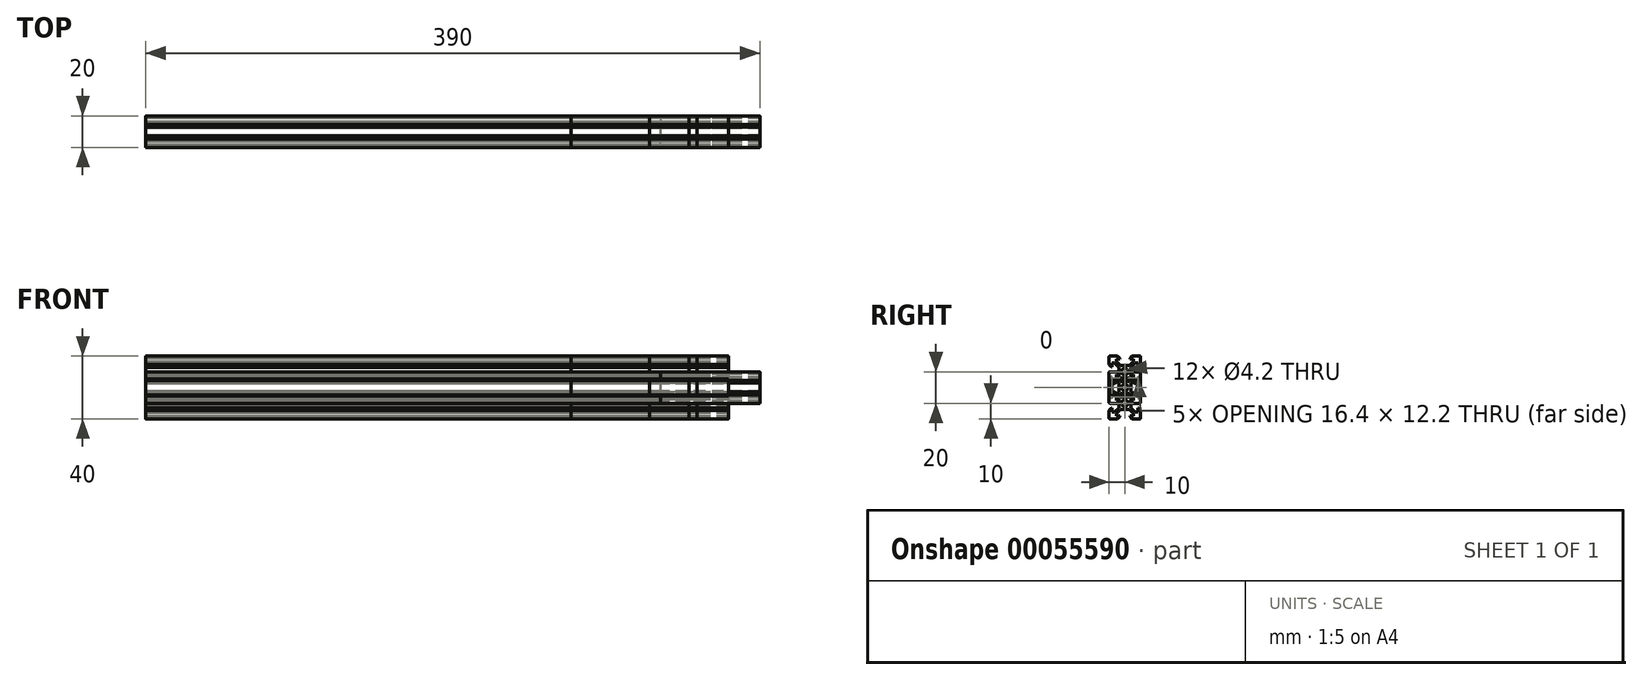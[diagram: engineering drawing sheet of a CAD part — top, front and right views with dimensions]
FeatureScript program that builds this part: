
annotation { "Feature Type Name" : "Feature", "Feature Type Description" : "" }
export const myFeature = defineFeature(function(context is Context, id is Id, definition is map)
    precondition{}
    {
        {
            var Q0;
            Q0=qCreatedBy(makeId("Right.planeOp"),FACE);
            var sketch = newSketch(context, id + "F0", { "sketchPlane" : qUnion([Q0]), "asVersion" : FeatureScriptVersionNumber.V275_SKETCH_PATTERN_LOWER_LIMIT});
            skLineSegment(sketch, "E0", {"start": v(0, 13.9) * mm, "end": v(-2.84, 13.9) * mm});
            skLineSegment(sketch, "E1", {"start": v(-2.84, 13.9) * mm, "end": v(-5.5, 16.56) * mm});
            skLineSegment(sketch, "E2", {"start": v(-5.5, 16.56) * mm, "end": v(-5.5, 18.2) * mm});
            skLineSegment(sketch, "E3", {"start": v(-5.5, 18.2) * mm, "end": v(-3.13, 18.2) * mm});
            skLineSegment(sketch, "E4", {"start": v(-3.13, 18.2) * mm, "end": v(-3.13, 18.55) * mm});
            skLineSegment(sketch, "E5", {"start": v(-3.13, 18.55) * mm, "end": v(-4.58, 20) * mm});
            skLineSegment(sketch, "E6", {"start": v(-4.58, 20) * mm, "end": v(-9.5, 20) * mm});
            skLineSegment(sketch, "E7", {"start": v(-10, 20) * mm, "end": v(0, 10) * mm, "construction": true});
            skLineSegment(sketch, "E8.MirrorCS", {"start": v(-3.9, 10) * mm, "end": v(-3.9, 12.84) * mm});
            skLineSegment(sketch, "E9.MirrorCS", {"start": v(-3.9, 12.84) * mm, "end": v(-6.56, 15.5) * mm});
            skLineSegment(sketch, "E10.MirrorCS", {"start": v(-6.56, 15.5) * mm, "end": v(-8.2, 15.5) * mm});
            skLineSegment(sketch, "E11.MirrorCS", {"start": v(-8.2, 15.5) * mm, "end": v(-8.2, 13.13) * mm});
            skLineSegment(sketch, "E12.MirrorCS", {"start": v(-8.2, 13.12) * mm, "end": v(-8.55, 13.12) * mm});
            skLineSegment(sketch, "E13.MirrorCS", {"start": v(-8.55, 13.13) * mm, "end": v(-10, 14.58) * mm});
            skLineSegment(sketch, "E14.MirrorCS", {"start": v(-10, 14.58) * mm, "end": v(-10, 19.5) * mm});
            skCircle(sketch, "E15", {"center": v(0, 10) * mm, "radius": 2.1 * mm});
            skPoint(sketch, "E16.visualSharp", {"position": v(-10, 20) * mm});
            skArc(sketch, "E16.filletArc", {"start": v(-9.5, 20) * mm, "mid": v(-9.85, 19.85) * mm, "end": v(-10, 19.5) * mm});
            skLineSegment(sketch, "E17", {"start": v(0, 10) * mm, "end": v(-3.9, 10) * mm, "construction": true});
            skLineSegment(sketch, "E18.MirrorCS", {"start": v(-3.9, 10) * mm, "end": v(-3.9, 7.16) * mm});
            skLineSegment(sketch, "E19.MirrorCS", {"start": v(0, 6.1) * mm, "end": v(-2.84, 6.1) * mm});
            skLineSegment(sketch, "E20.MirrorCS", {"start": v(-3.9, 7.16) * mm, "end": v(-6.56, 4.5) * mm});
            skLineSegment(sketch, "E21.MirrorCS", {"start": v(-6.56, 4.5) * mm, "end": v(-8.2, 4.5) * mm});
            skLineSegment(sketch, "E22.MirrorCS", {"start": v(-8.2, 4.5) * mm, "end": v(-8.2, 6.87) * mm});
            skLineSegment(sketch, "E23.MirrorCS", {"start": v(-8.2, 6.87) * mm, "end": v(-8.55, 6.87) * mm});
            skLineSegment(sketch, "E24.MirrorCS", {"start": v(-8.55, 6.87) * mm, "end": v(-10, 5.42) * mm});
            skLineSegment(sketch, "E25", {"start": v(-10, 5.42) * mm, "end": v(-10, 0) * mm});
            skLineSegment(sketch, "E26", {"start": v(-2.84, 6.1) * mm, "end": v(-6.24, 2.7) * mm});
            skLineSegment(sketch, "E27", {"start": v(-6.24, 2.7) * mm, "end": v(-8.2, 2.7) * mm});
            skLineSegment(sketch, "E28", {"start": v(-8.2, 2.7) * mm, "end": v(-8.2, 0) * mm});
            skLineSegment(sketch, "E29.MirrorCS", {"start": v(0, 13.9) * mm, "end": v(2.84, 13.9) * mm});
            skLineSegment(sketch, "E30.MirrorCS", {"start": v(2.84, 13.9) * mm, "end": v(5.5, 16.56) * mm});
            skLineSegment(sketch, "E31.MirrorCS", {"start": v(5.5, 16.56) * mm, "end": v(5.5, 18.2) * mm});
            skLineSegment(sketch, "E32.MirrorCS", {"start": v(5.5, 18.2) * mm, "end": v(3.13, 18.2) * mm});
            skLineSegment(sketch, "E33.MirrorCS", {"start": v(3.13, 18.2) * mm, "end": v(3.13, 18.55) * mm});
            skLineSegment(sketch, "E34.MirrorCS", {"start": v(3.13, 18.55) * mm, "end": v(4.58, 20) * mm});
            skLineSegment(sketch, "E35.MirrorCS", {"start": v(4.58, 20) * mm, "end": v(9.5, 20) * mm});
            skArc(sketch, "E36.MirrorCS", {"start": v(9.5, 20) * mm, "mid": v(9.85, 19.85) * mm, "end": v(10, 19.5) * mm});
            skLineSegment(sketch, "E37.MirrorCS", {"start": v(10, 14.58) * mm, "end": v(10, 19.5) * mm});
            skLineSegment(sketch, "E38.MirrorCS", {"start": v(8.55, 13.13) * mm, "end": v(10, 14.58) * mm});
            skLineSegment(sketch, "E39.MirrorCS", {"start": v(8.2, 13.12) * mm, "end": v(8.55, 13.12) * mm});
            skLineSegment(sketch, "E40.MirrorCS", {"start": v(8.2, 15.5) * mm, "end": v(8.2, 13.13) * mm});
            skLineSegment(sketch, "E41.MirrorCS", {"start": v(6.56, 15.5) * mm, "end": v(8.2, 15.5) * mm});
            skLineSegment(sketch, "E42.MirrorCS", {"start": v(3.9, 12.84) * mm, "end": v(6.56, 15.5) * mm});
            skLineSegment(sketch, "E43.MirrorCS", {"start": v(3.9, 10) * mm, "end": v(3.9, 12.84) * mm});
            skLineSegment(sketch, "E44.MirrorCS", {"start": v(3.9, 10) * mm, "end": v(3.9, 7.16) * mm});
            skLineSegment(sketch, "E45.MirrorCS", {"start": v(3.9, 7.16) * mm, "end": v(6.56, 4.5) * mm});
            skLineSegment(sketch, "E46.MirrorCS", {"start": v(6.56, 4.5) * mm, "end": v(8.2, 4.5) * mm});
            skLineSegment(sketch, "E47.MirrorCS", {"start": v(8.2, 4.5) * mm, "end": v(8.2, 6.87) * mm});
            skLineSegment(sketch, "E48.MirrorCS", {"start": v(8.2, 6.87) * mm, "end": v(8.55, 6.87) * mm});
            skLineSegment(sketch, "E49.MirrorCS", {"start": v(8.55, 6.87) * mm, "end": v(10, 5.42) * mm});
            skLineSegment(sketch, "E50.MirrorCS", {"start": v(10, 5.42) * mm, "end": v(10, 0) * mm});
            skLineSegment(sketch, "E51.MirrorCS", {"start": v(0, 6.1) * mm, "end": v(2.84, 6.1) * mm});
            skLineSegment(sketch, "E52.MirrorCS", {"start": v(2.84, 6.1) * mm, "end": v(6.24, 2.7) * mm});
            skLineSegment(sketch, "E53.MirrorCS", {"start": v(6.24, 2.7) * mm, "end": v(8.2, 2.7) * mm});
            skLineSegment(sketch, "E54.MirrorCS", {"start": v(8.2, 2.7) * mm, "end": v(8.2, 0) * mm});
            skLineSegment(sketch, "E55.MirrorCS", {"start": v(8.2, -2.7) * mm, "end": v(8.2, 0) * mm});
            skLineSegment(sketch, "E56.MirrorCS", {"start": v(6.24, -2.7) * mm, "end": v(8.2, -2.7) * mm});
            skLineSegment(sketch, "E57.MirrorCS", {"start": v(2.84, -6.1) * mm, "end": v(6.24, -2.7) * mm});
            skLineSegment(sketch, "E58.MirrorCS", {"start": v(0, -6.1) * mm, "end": v(2.84, -6.1) * mm});
            skLineSegment(sketch, "E59.MirrorCS", {"start": v(0, -6.1) * mm, "end": v(-2.84, -6.1) * mm});
            skLineSegment(sketch, "E60.MirrorCS", {"start": v(-2.84, -6.1) * mm, "end": v(-6.24, -2.7) * mm});
            skLineSegment(sketch, "E61.MirrorCS", {"start": v(-6.24, -2.7) * mm, "end": v(-8.2, -2.7) * mm});
            skLineSegment(sketch, "E62.MirrorCS", {"start": v(-8.2, -2.7) * mm, "end": v(-8.2, 0) * mm});
            skLineSegment(sketch, "E63.MirrorCS", {"start": v(10, -5.42) * mm, "end": v(10, 0) * mm});
            skLineSegment(sketch, "E64.MirrorCS", {"start": v(8.55, -6.87) * mm, "end": v(10, -5.42) * mm});
            skLineSegment(sketch, "E65.MirrorCS", {"start": v(8.2, -6.87) * mm, "end": v(8.55, -6.87) * mm});
            skLineSegment(sketch, "E66.MirrorCS", {"start": v(8.2, -4.5) * mm, "end": v(8.2, -6.87) * mm});
            skLineSegment(sketch, "E67.MirrorCS", {"start": v(6.56, -4.5) * mm, "end": v(8.2, -4.5) * mm});
            skLineSegment(sketch, "E68.MirrorCS", {"start": v(3.9, -7.16) * mm, "end": v(6.56, -4.5) * mm});
            skLineSegment(sketch, "E69.MirrorCS", {"start": v(3.9, -10) * mm, "end": v(3.9, -7.16) * mm});
            skLineSegment(sketch, "E70.MirrorCS", {"start": v(3.9, -10) * mm, "end": v(3.9, -12.84) * mm});
            skLineSegment(sketch, "E71.MirrorCS", {"start": v(3.9, -12.84) * mm, "end": v(6.56, -15.5) * mm});
            skLineSegment(sketch, "E72.MirrorCS", {"start": v(6.56, -15.5) * mm, "end": v(8.2, -15.5) * mm});
            skLineSegment(sketch, "E73.MirrorCS", {"start": v(8.2, -15.5) * mm, "end": v(8.2, -13.13) * mm});
            skLineSegment(sketch, "E74.MirrorCS", {"start": v(8.2, -13.12) * mm, "end": v(8.55, -13.12) * mm});
            skLineSegment(sketch, "E75.MirrorCS", {"start": v(8.55, -13.13) * mm, "end": v(10, -14.58) * mm});
            skLineSegment(sketch, "E76.MirrorCS", {"start": v(10, -14.58) * mm, "end": v(10, -19.5) * mm});
            skArc(sketch, "E77.MirrorCS", {"start": v(9.5, -20) * mm, "mid": v(9.85, -19.85) * mm, "end": v(10, -19.5) * mm});
            skLineSegment(sketch, "E78.MirrorCS", {"start": v(4.58, -20) * mm, "end": v(9.5, -20) * mm});
            skLineSegment(sketch, "E79.MirrorCS", {"start": v(3.13, -18.55) * mm, "end": v(4.58, -20) * mm});
            skLineSegment(sketch, "E80.MirrorCS", {"start": v(3.13, -18.2) * mm, "end": v(3.13, -18.55) * mm});
            skLineSegment(sketch, "E81.MirrorCS", {"start": v(5.5, -18.2) * mm, "end": v(3.13, -18.2) * mm});
            skLineSegment(sketch, "E82.MirrorCS", {"start": v(5.5, -16.56) * mm, "end": v(5.5, -18.2) * mm});
            skLineSegment(sketch, "E83.MirrorCS", {"start": v(2.84, -13.9) * mm, "end": v(5.5, -16.56) * mm});
            skLineSegment(sketch, "E84.MirrorCS", {"start": v(0, -13.9) * mm, "end": v(2.84, -13.9) * mm});
            skLineSegment(sketch, "E85.MirrorCS", {"start": v(0, -13.9) * mm, "end": v(-2.84, -13.9) * mm});
            skLineSegment(sketch, "E86.MirrorCS", {"start": v(-2.84, -13.9) * mm, "end": v(-5.5, -16.56) * mm});
            skLineSegment(sketch, "E87.MirrorCS", {"start": v(-5.5, -16.56) * mm, "end": v(-5.5, -18.2) * mm});
            skLineSegment(sketch, "E88.MirrorCS", {"start": v(-5.5, -18.2) * mm, "end": v(-3.13, -18.2) * mm});
            skLineSegment(sketch, "E89.MirrorCS", {"start": v(-3.13, -18.2) * mm, "end": v(-3.13, -18.55) * mm});
            skLineSegment(sketch, "E90.MirrorCS", {"start": v(-3.13, -18.55) * mm, "end": v(-4.58, -20) * mm});
            skLineSegment(sketch, "E91.MirrorCS", {"start": v(-4.58, -20) * mm, "end": v(-9.5, -20) * mm});
            skArc(sketch, "E92.MirrorCS", {"start": v(-9.5, -20) * mm, "mid": v(-9.85, -19.85) * mm, "end": v(-10, -19.5) * mm});
            skLineSegment(sketch, "E93.MirrorCS", {"start": v(-10, -14.58) * mm, "end": v(-10, -19.5) * mm});
            skLineSegment(sketch, "E94.MirrorCS", {"start": v(-8.55, -13.13) * mm, "end": v(-10, -14.58) * mm});
            skLineSegment(sketch, "E95.MirrorCS", {"start": v(-8.2, -13.12) * mm, "end": v(-8.55, -13.12) * mm});
            skLineSegment(sketch, "E96.MirrorCS", {"start": v(-8.2, -15.5) * mm, "end": v(-8.2, -13.13) * mm});
            skLineSegment(sketch, "E97.MirrorCS", {"start": v(-6.56, -15.5) * mm, "end": v(-8.2, -15.5) * mm});
            skLineSegment(sketch, "E98.MirrorCS", {"start": v(-3.9, -12.84) * mm, "end": v(-6.56, -15.5) * mm});
            skLineSegment(sketch, "E99.MirrorCS", {"start": v(-3.9, -10) * mm, "end": v(-3.9, -12.84) * mm});
            skLineSegment(sketch, "E100.MirrorCS", {"start": v(-3.9, -10) * mm, "end": v(-3.9, -7.16) * mm});
            skLineSegment(sketch, "E101.MirrorCS", {"start": v(-3.9, -7.16) * mm, "end": v(-6.56, -4.5) * mm});
            skLineSegment(sketch, "E102.MirrorCS", {"start": v(-6.56, -4.5) * mm, "end": v(-8.2, -4.5) * mm});
            skLineSegment(sketch, "E103.MirrorCS", {"start": v(-8.2, -4.5) * mm, "end": v(-8.2, -6.87) * mm});
            skLineSegment(sketch, "E104.MirrorCS", {"start": v(-8.2, -6.87) * mm, "end": v(-8.55, -6.87) * mm});
            skLineSegment(sketch, "E105.MirrorCS", {"start": v(-8.55, -6.87) * mm, "end": v(-10, -5.42) * mm});
            skLineSegment(sketch, "E106.MirrorCS", {"start": v(-10, -5.42) * mm, "end": v(-10, 0) * mm});
            skCircle(sketch, "E107.MirrorC", {"center": v(0, -10) * mm, "radius": 2.1 * mm});
            skSolve(sketch);
        }
        {
            var Q0;
            Q0=qCreatedBy(makeId("Right.planeOp"),FACE);
            var sketch = newSketch(context, id + "F1", { "sketchPlane" : qUnion([Q0]), "asVersion" : FeatureScriptVersionNumber.V275_SKETCH_PATTERN_LOWER_LIMIT});
            skLineSegment(sketch, "E108", {"start": v(0, 0) * mm, "end": v(-10, 10) * mm, "construction": true});
            skLineSegment(sketch, "E109", {"start": v(-9.5, 10) * mm, "end": v(-4.58, 10) * mm});
            skLineSegment(sketch, "E110", {"start": v(-4.58, 10) * mm, "end": v(-3.12, 8.54) * mm});
            skLineSegment(sketch, "E111", {"start": v(-3.12, 8.54) * mm, "end": v(-3.12, 8.2) * mm});
            skLineSegment(sketch, "E112", {"start": v(-3.12, 8.2) * mm, "end": v(-5.5, 8.2) * mm});
            skLineSegment(sketch, "E113", {"start": v(-5.5, 8.2) * mm, "end": v(-5.5, 6.56) * mm});
            skLineSegment(sketch, "E114", {"start": v(-5.5, 6.56) * mm, "end": v(-2.84, 3.9) * mm});
            skLineSegment(sketch, "E115", {"start": v(-2.84, 3.9) * mm, "end": v(0, 3.9) * mm});
            skLineSegment(sketch, "E116.MirrorCS", {"start": v(-10, 9.5) * mm, "end": v(-10, 4.58) * mm});
            skLineSegment(sketch, "E117.MirrorCS", {"start": v(-10, 4.58) * mm, "end": v(-8.54, 3.12) * mm});
            skLineSegment(sketch, "E118.MirrorCS", {"start": v(-8.54, 3.12) * mm, "end": v(-8.2, 3.12) * mm});
            skLineSegment(sketch, "E119.MirrorCS", {"start": v(-8.2, 3.12) * mm, "end": v(-8.2, 5.5) * mm});
            skLineSegment(sketch, "E120.MirrorCS", {"start": v(-8.2, 5.5) * mm, "end": v(-6.56, 5.5) * mm});
            skLineSegment(sketch, "E121.MirrorCS", {"start": v(-6.56, 5.5) * mm, "end": v(-3.9, 2.84) * mm});
            skLineSegment(sketch, "E122.MirrorCS", {"start": v(-3.9, 2.84) * mm, "end": v(-3.9, 0) * mm});
            skPoint(sketch, "E123.visualSharp", {"position": v(-10, 10) * mm});
            skArc(sketch, "E123.filletArc", {"start": v(-9.5, 10) * mm, "mid": v(-9.85, 9.85) * mm, "end": v(-10, 9.5) * mm});
            skLineSegment(sketch, "E124.MirrorCS", {"start": v(2.84, 3.9) * mm, "end": v(0, 3.9) * mm});
            skLineSegment(sketch, "E125.MirrorCS", {"start": v(5.5, 6.56) * mm, "end": v(2.84, 3.9) * mm});
            skLineSegment(sketch, "E126.MirrorCS", {"start": v(5.5, 8.2) * mm, "end": v(5.5, 6.56) * mm});
            skLineSegment(sketch, "E127.MirrorCS", {"start": v(3.12, 8.2) * mm, "end": v(5.5, 8.2) * mm});
            skLineSegment(sketch, "E128.MirrorCS", {"start": v(3.12, 8.54) * mm, "end": v(3.12, 8.2) * mm});
            skLineSegment(sketch, "E129.MirrorCS", {"start": v(4.58, 10) * mm, "end": v(3.12, 8.54) * mm});
            skLineSegment(sketch, "E130.MirrorCS", {"start": v(9.5, 10) * mm, "end": v(4.58, 10) * mm});
            skArc(sketch, "E131.MirrorCS", {"start": v(9.5, 10) * mm, "mid": v(9.85, 9.85) * mm, "end": v(10, 9.5) * mm});
            skLineSegment(sketch, "E132.MirrorCS", {"start": v(10, 9.5) * mm, "end": v(10, 4.58) * mm});
            skLineSegment(sketch, "E133.MirrorCS", {"start": v(10, 4.58) * mm, "end": v(8.54, 3.13) * mm});
            skLineSegment(sketch, "E134.MirrorCS", {"start": v(8.54, 3.12) * mm, "end": v(8.2, 3.12) * mm});
            skLineSegment(sketch, "E135.MirrorCS", {"start": v(8.2, 3.12) * mm, "end": v(8.2, 5.5) * mm});
            skLineSegment(sketch, "E136.MirrorCS", {"start": v(8.2, 5.5) * mm, "end": v(6.56, 5.5) * mm});
            skLineSegment(sketch, "E137.MirrorCS", {"start": v(6.56, 5.5) * mm, "end": v(3.9, 2.84) * mm});
            skLineSegment(sketch, "E138.MirrorCS", {"start": v(3.9, 2.84) * mm, "end": v(3.9, 0) * mm});
            skLineSegment(sketch, "E139.MirrorCS", {"start": v(-3.9, -2.84) * mm, "end": v(-3.9, 0) * mm});
            skLineSegment(sketch, "E140.MirrorCS", {"start": v(-6.56, -5.5) * mm, "end": v(-3.9, -2.84) * mm});
            skLineSegment(sketch, "E141.MirrorCS", {"start": v(-8.2, -5.5) * mm, "end": v(-6.56, -5.5) * mm});
            skLineSegment(sketch, "E142.MirrorCS", {"start": v(-8.2, -3.12) * mm, "end": v(-8.2, -5.5) * mm});
            skLineSegment(sketch, "E143.MirrorCS", {"start": v(-8.54, -3.12) * mm, "end": v(-8.2, -3.12) * mm});
            skLineSegment(sketch, "E144.MirrorCS", {"start": v(-10, -4.58) * mm, "end": v(-8.54, -3.13) * mm});
            skLineSegment(sketch, "E145.MirrorCS", {"start": v(-10, -9.5) * mm, "end": v(-10, -4.58) * mm});
            skArc(sketch, "E146.MirrorCS", {"start": v(-9.5, -10) * mm, "mid": v(-9.85, -9.85) * mm, "end": v(-10, -9.5) * mm});
            skLineSegment(sketch, "E147.MirrorCS", {"start": v(-9.5, -10) * mm, "end": v(-4.58, -10) * mm});
            skLineSegment(sketch, "E148.MirrorCS", {"start": v(-4.58, -10) * mm, "end": v(-3.12, -8.54) * mm});
            skLineSegment(sketch, "E149.MirrorCS", {"start": v(-3.12, -8.54) * mm, "end": v(-3.12, -8.2) * mm});
            skLineSegment(sketch, "E150.MirrorCS", {"start": v(-3.12, -8.2) * mm, "end": v(-5.5, -8.2) * mm});
            skLineSegment(sketch, "E151.MirrorCS", {"start": v(-5.5, -8.2) * mm, "end": v(-5.5, -6.56) * mm});
            skLineSegment(sketch, "E152.MirrorCS", {"start": v(-5.5, -6.56) * mm, "end": v(-2.84, -3.9) * mm});
            skLineSegment(sketch, "E153.MirrorCS", {"start": v(-2.84, -3.9) * mm, "end": v(0, -3.9) * mm});
            skLineSegment(sketch, "E154.MirrorCS", {"start": v(2.84, -3.9) * mm, "end": v(0, -3.9) * mm});
            skLineSegment(sketch, "E155.MirrorCS", {"start": v(5.5, -6.56) * mm, "end": v(2.84, -3.9) * mm});
            skLineSegment(sketch, "E156.MirrorCS", {"start": v(5.5, -8.2) * mm, "end": v(5.5, -6.56) * mm});
            skLineSegment(sketch, "E157.MirrorCS", {"start": v(3.12, -8.2) * mm, "end": v(5.5, -8.2) * mm});
            skLineSegment(sketch, "E158.MirrorCS", {"start": v(3.13, -8.54) * mm, "end": v(3.13, -8.2) * mm});
            skLineSegment(sketch, "E159.MirrorCS", {"start": v(4.58, -10) * mm, "end": v(3.12, -8.54) * mm});
            skLineSegment(sketch, "E160.MirrorCS", {"start": v(9.5, -10) * mm, "end": v(4.58, -10) * mm});
            skArc(sketch, "E161.MirrorCS", {"start": v(9.5, -10) * mm, "mid": v(9.85, -9.85) * mm, "end": v(10, -9.5) * mm});
            skLineSegment(sketch, "E162.MirrorCS", {"start": v(10, -9.5) * mm, "end": v(10, -4.58) * mm});
            skLineSegment(sketch, "E163.MirrorCS", {"start": v(10, -4.58) * mm, "end": v(8.54, -3.12) * mm});
            skLineSegment(sketch, "E164.MirrorCS", {"start": v(8.54, -3.12) * mm, "end": v(8.2, -3.12) * mm});
            skLineSegment(sketch, "E165.MirrorCS", {"start": v(8.2, -3.12) * mm, "end": v(8.2, -5.5) * mm});
            skLineSegment(sketch, "E166.MirrorCS", {"start": v(8.2, -5.5) * mm, "end": v(6.56, -5.5) * mm});
            skLineSegment(sketch, "E167.MirrorCS", {"start": v(6.56, -5.5) * mm, "end": v(3.9, -2.84) * mm});
            skLineSegment(sketch, "E168.MirrorCS", {"start": v(3.9, -2.84) * mm, "end": v(3.9, 0) * mm});
            skCircle(sketch, "E169", {"center": v(0, 0) * mm, "radius": 2.1 * mm});
            skSolve(sketch);
        }
        {
            var Q0;
            Q0=makeQuery(id+"F0.imprint","IMPRINT",FACE,{"disambiguationData":[TD([[makeQuery(id+"F0.imprint","IMPRINT",EDGE,{"derivedFrom":sQuery(id+"F0.wireOp",EDGE,"E0")}),1.0]])]});
            extrude(context, id + "F2", {"entities" : qUnion([Q0]), "depth" : 345 * mm});
        }
        {
            var Q0;
            Q0=makeQuery(id+"F0.imprint","IMPRINT",FACE,{"disambiguationData":[TD([[makeQuery(id+"F0.imprint","IMPRINT",EDGE,{"derivedFrom":sQuery(id+"F0.wireOp",EDGE,"E0")}),1.0]])]});
            extrude(context, id + "F3", {"entities" : qUnion([Q0]), "depth" : 270 * mm});
        }
        {
            var Q0;
            Q0=qSketchRegion(id+"F0",true);
            extrude(context, id + "F4", {"entities" : qUnion([Q0]), "depth" : 320 * mm});
        }
        {
            var Q0;
            Q0=qSketchRegion(id+"F1",true);
            extrude(context, id + "F5", {"entities" : qUnion([Q0]), "depth" : 327 * mm});
        }
        {
            var Q0;
            Q0=qSketchRegion(id+"F0",true);
            extrude(context, id + "F6", {"entities" : qUnion([Q0]), "depth" : 370 * mm});
        }
        {
            var Q0;
            Q0=qSketchRegion(id+"F1",true);
            extrude(context, id + "F7", {"entities" : qUnion([Q0]), "depth" : 390 * mm});
        }
        {
            var Q0;
            Q0=qSketchRegion(id+"F0",true);
            extrude(context, id + "F8", {"entities" : qUnion([Q0]), "depth" : 350 * mm});
        }
    });
